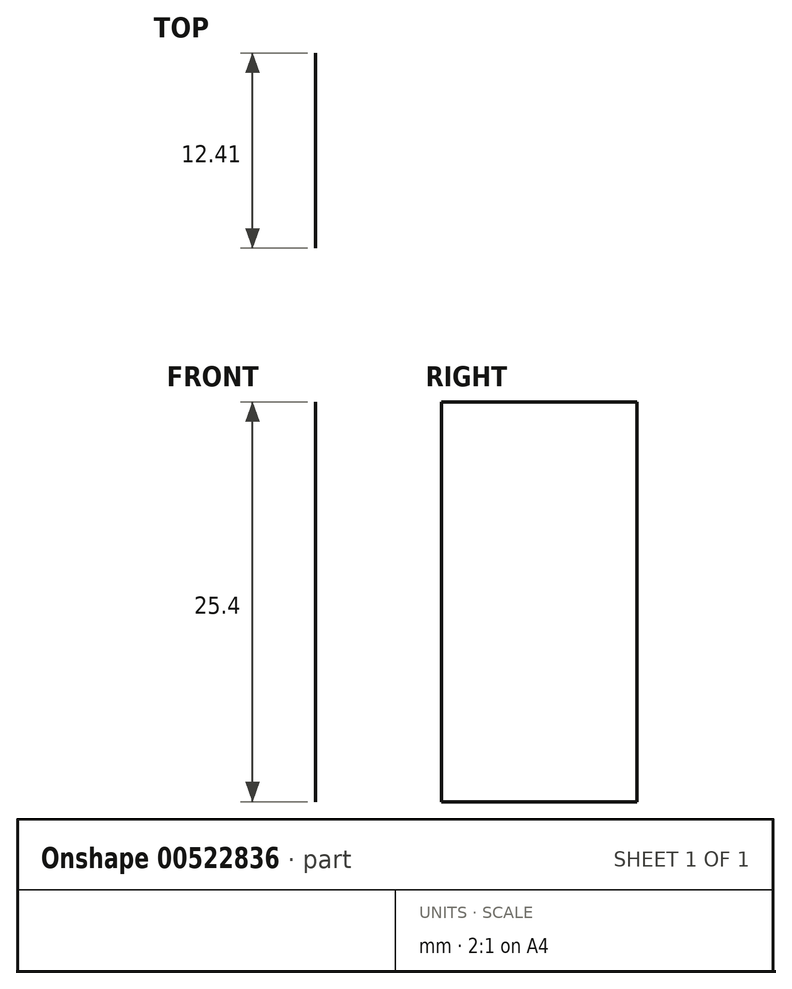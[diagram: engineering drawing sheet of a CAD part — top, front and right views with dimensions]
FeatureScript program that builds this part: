
annotation { "Feature Type Name" : "Feature", "Feature Type Description" : "" }
export const myFeature = defineFeature(function(context is Context, id is Id, definition is map)
    precondition{}
    {
        {
            var Q0;
            Q0=qCreatedBy(makeId("Top.planeOp"),FACE);
            var sketch = newSketch(context, id + "F0", { "sketchPlane" : qUnion([Q0])});
            skLineSegment(sketch, "E0", {"start": v(-19.2, 0) * mm, "end": v(-19.2, -12.4) * mm});
            skSolve(sketch);
        }
        {
            var Q0;
            Q0=sQuery(id+"F0.wireOp",EDGE,"E0");
            extrude(context, id + "F1", {"bodyType" : ToolBodyType.SURFACE, "surfaceEntities" : qUnion([Q0]), "depth" : 25.4 * mm, "offsetDistance" : 25.4 * mm});
        }
    });
